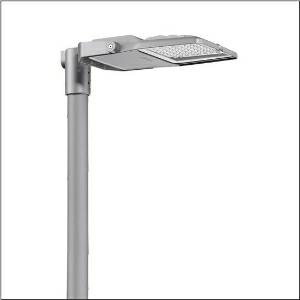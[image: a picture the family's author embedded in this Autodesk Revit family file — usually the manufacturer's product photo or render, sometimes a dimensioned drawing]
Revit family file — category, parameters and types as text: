
# Revit family: floodlight_fl_21_iq_mini___pl64_5xa7771c2e3a_b06c
name_source: partatom
category: Lighting Fixtures
units: mm (PartAtom-declared; Revit-internal decimal feet)

## family parameters
Cut with Voids When Loaded = No
Host = Face
Light Source = No
Part Type = Normal
Room Calculation Point = No
Round Connector Dimension = Use Diameter
Shared = No

## types (1)
- --- (1 x LED, 11790 lm, 87.2 W, 3000K)
    Apparent Load = 87 VA
    CIE Flux Codes = 28 80 98 100 100
    Color Rendering = 70
    Color Temperature = 3000K
    Default Elevation = 1800 mm
    Description = Floodlight FL 21 iQ mini, floodlight, primary light control with lens, of PMMA, primary optical cover: protective disc, of toughened safety glass, transparent, light distribution: PL64, light emission: direct distribution, installation type: surface-mounted, lamps: LED, High Power LED, rated values: 11.790lm | 87,2W | 135,2lm/W (begin service life); end service life: 11.790lm | 92,1W; at 50% lumin. flux: 5.895lm | 40,1W | 147lm/W, colour temperature: 3000K, colour rendering: CRI > 70, light colour: 730, light setting 1 begin service life: 100% | 11.790lm | 87,2W | 135,2lm/W | 3.000K, light setting 1 end service life: 92,1W, further light settings possible, control: Auto-Match, Temp-Guard, Lumen-Switch, Night-Set, Smart-Wire, Light-Fading, Desk-Remote (wireless, voltage-free reading and setting of iQ features in the workshop via application-optimized NFC function/RFID function), optimised constant luminous flux control (CLO 2.0), pre-setting: linear dimming characteristic, with terminal, 6-pole, mains connection: 220..240V, AC, 50/60Hz, luminaire housing, of diecast aluminium, powder-coated, SITECO metallic grey (DB 702S), corrosivity category C5 mid according to DIN EN ISO 12944suitable for swimming poolschlorine-resistant, sealing non-destructively replaceable, please order mast flange separately, mast bracket, of steel, galvanised, powder-coated, SITECO metallic grey (DB 702S), protection rating (complete): IP66, insulation class (complete): insulation class II (safety insulation), certification: CE, ENEC, VDE, protection symbol: D, impact resistance: IK08, permissible operating ambient temperature: -40..+40°C, permissible operating ambient temperature for outdoor applications: -40..+50°C, standard: DIN EN 12944, LABS conformity tested according to VDMA 24364:2018-05, packaging unit: 1 piece

Light Distribution: PL64
    Height = 70 mm
    Lamp = 1 x LED
    Lamp Light Flux = 11790 lm
    Lamp Power = 87.2 W
    Lamp count = 1
    Length = 485 mm
    Luminous efficacy = 135 lm/W
    Manufacturer = Siteco
    ModVariant = No
    Model = 5XA7771C2E3A
    Number of Poles = 1
    OnlyDefault = Yes
    Power Factor = 1
    Product Name = Floodlight FL 21 iQ mini | PL64
    Product group = floodlight | pylon annexe
    ProductGroupID = 6201
    Protection Class = Protection class II
    Protection Degree = IP 66
    RLX_Detail_Level = 1
    RLX_Emergency_Light_Flux = 0 lm
    RLX_Emergency_Type = 0
    RLX_Emergency_Type_DB = No
    RlxData = <blob elided: 101561 chars, md5=6d9aaa27>
    Socket = socket
    Standby Power = 0 W
    System Light Flux = 11790 lm
    System Power = 87 W
    Type Comments = factory setting: luminous flux: 100 % | dim-lin: 254 | 456 mA
    Type Image = l_1007125.jpg
    URL = http://relux.com
    VarID = @adj_166091
    Voltage = 0 V
    Weight = 0.00 kg
    Width = 337 mm

## geometry (parser evidence)
native form markers: Blend x4, Sweep x11
no freeform markers — native parametric forms only
